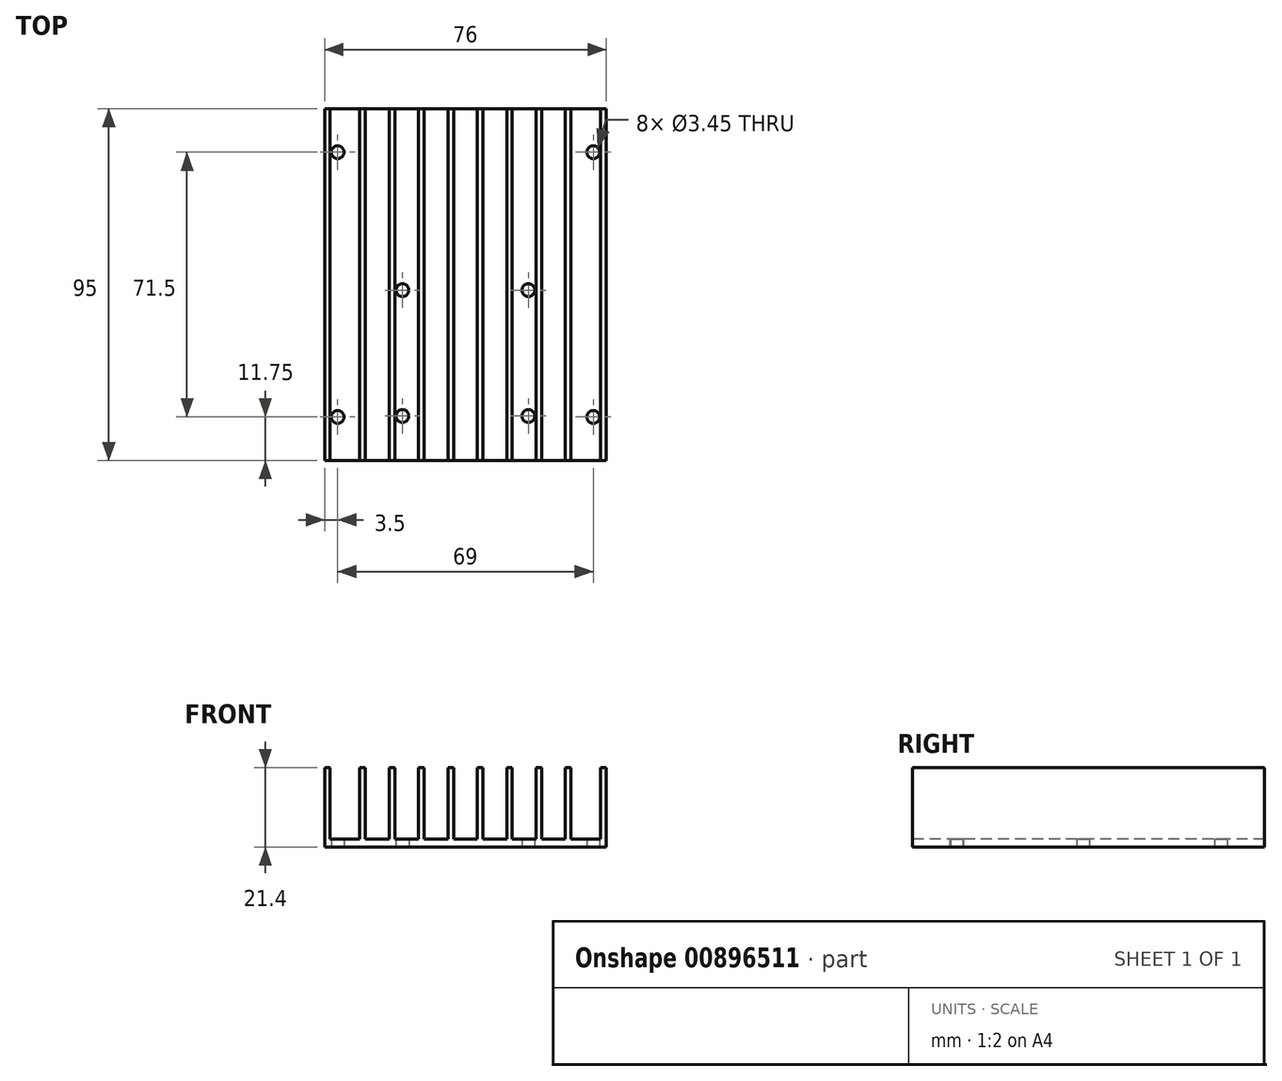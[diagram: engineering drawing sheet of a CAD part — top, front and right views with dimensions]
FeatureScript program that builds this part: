
annotation { "Feature Type Name" : "Feature", "Feature Type Description" : "" }
export const myFeature = defineFeature(function(context is Context, id is Id, definition is map)
    precondition{}
    {
        {
            var Q0;
            Q0=qCreatedBy(makeId("Top.planeOp"),FACE);
            var sketch = newSketch(context, id + "F0", { "sketchPlane" : qUnion([Q0])});
            skLineSegment(sketch, "E0.bottom", {"start": v(38, 47.5) * mm, "end": v(-38, 47.5) * mm});
            skLineSegment(sketch, "E0.top", {"start": v(38, -47.5) * mm, "end": v(-38, -47.5) * mm});
            skLineSegment(sketch, "E0.left", {"start": v(38, 47.5) * mm, "end": v(38, -47.5) * mm});
            skLineSegment(sketch, "E0.right", {"start": v(-38, 47.5) * mm, "end": v(-38, -47.5) * mm});
            skPoint(sketch, "E0.middle", {"position": v(0, 0) * mm});
            skSolve(sketch);
        }
        {
            var Q0;
            Q0 = qSketchRegion(id + "F0", true);
            extrude(context, id + "F1", {"entities" : qUnion([Q0]), "depth" : 21.4 * mm, "offsetDistance" : 25 * mm});
        }
        {
            var Q0;
            Q0=makeQuery(id+"F1.opExtrude","SWEPT_FACE",FACE,{"disambiguationData":[OSD([sQuery(id+"F0.wireOp",EDGE,"E0.top")])]});
            var sketch = newSketch(context, id + "F2", { "sketchPlane" : qUnion([Q0])});
            skLineSegment(sketch, "E1.bottom", {"start": v(-36.5, 21.4) * mm, "end": v(-28.5, 21.4) * mm});
            skLineSegment(sketch, "E1.top", {"start": v(-36.5, 2.1) * mm, "end": v(-28.5, 2.1) * mm});
            skLineSegment(sketch, "E1.left", {"start": v(-36.5, 21.4) * mm, "end": v(-36.5, 2.1) * mm});
            skLineSegment(sketch, "E1.right", {"start": v(-28.5, 21.4) * mm, "end": v(-28.5, 2.1) * mm});
            skLineSegment(sketch, "E2.bottom", {"start": v(28.5, 21.4) * mm, "end": v(36.5, 21.4) * mm});
            skLineSegment(sketch, "E2.top", {"start": v(28.5, 2.1) * mm, "end": v(36.5, 2.1) * mm});
            skLineSegment(sketch, "E2.left", {"start": v(28.5, 21.4) * mm, "end": v(28.5, 2.1) * mm});
            skLineSegment(sketch, "E2.right", {"start": v(36.5, 21.4) * mm, "end": v(36.5, 2.1) * mm});
            skLineSegment(sketch, "E3.bottom", {"start": v(-27, 21.4) * mm, "end": v(-20.57, 21.4) * mm});
            skLineSegment(sketch, "E3.top", {"start": v(-27, 2.1) * mm, "end": v(-20.57, 2.1) * mm});
            skLineSegment(sketch, "E3.left", {"start": v(-27, 21.4) * mm, "end": v(-27, 2.1) * mm});
            skLineSegment(sketch, "E3.right", {"start": v(-20.57, 21.4) * mm, "end": v(-20.57, 2.1) * mm});
            skLineSegment(sketch, "E4.bottom", {"start": v(-19.07, 21.4) * mm, "end": v(-12.64, 21.4) * mm});
            skLineSegment(sketch, "E4.top", {"start": v(-19.07, 2.1) * mm, "end": v(-12.64, 2.1) * mm});
            skLineSegment(sketch, "E4.left", {"start": v(-19.07, 21.4) * mm, "end": v(-19.07, 2.1) * mm});
            skLineSegment(sketch, "E4.right", {"start": v(-12.64, 21.4) * mm, "end": v(-12.64, 2.1) * mm});
            skLineSegment(sketch, "E5.bottom", {"start": v(-11.14, 21.4) * mm, "end": v(-4.71, 21.4) * mm});
            skLineSegment(sketch, "E5.top", {"start": v(-11.14, 2.1) * mm, "end": v(-4.71, 2.1) * mm});
            skLineSegment(sketch, "E5.left", {"start": v(-11.14, 21.4) * mm, "end": v(-11.14, 2.1) * mm});
            skLineSegment(sketch, "E5.right", {"start": v(-4.71, 21.4) * mm, "end": v(-4.71, 2.1) * mm});
            skLineSegment(sketch, "E6.bottom", {"start": v(-3.21, 21.4) * mm, "end": v(3.21, 21.4) * mm});
            skLineSegment(sketch, "E6.top", {"start": v(-3.21, 2.1) * mm, "end": v(3.21, 2.1) * mm});
            skLineSegment(sketch, "E6.left", {"start": v(-3.21, 21.4) * mm, "end": v(-3.21, 2.1) * mm});
            skLineSegment(sketch, "E6.right", {"start": v(3.21, 21.4) * mm, "end": v(3.21, 2.1) * mm});
            skLineSegment(sketch, "E7.bottom", {"start": v(4.71, 21.4) * mm, "end": v(11.14, 21.4) * mm});
            skLineSegment(sketch, "E7.top", {"start": v(4.71, 2.1) * mm, "end": v(11.14, 2.1) * mm});
            skLineSegment(sketch, "E7.left", {"start": v(4.71, 21.4) * mm, "end": v(4.71, 2.1) * mm});
            skLineSegment(sketch, "E7.right", {"start": v(11.14, 21.4) * mm, "end": v(11.14, 2.1) * mm});
            skLineSegment(sketch, "E8.bottom", {"start": v(12.64, 21.4) * mm, "end": v(19.07, 21.4) * mm});
            skLineSegment(sketch, "E8.top", {"start": v(12.64, 2.1) * mm, "end": v(19.07, 2.1) * mm});
            skLineSegment(sketch, "E8.left", {"start": v(12.64, 21.4) * mm, "end": v(12.64, 2.1) * mm});
            skLineSegment(sketch, "E8.right", {"start": v(19.07, 21.4) * mm, "end": v(19.07, 2.1) * mm});
            skLineSegment(sketch, "E9.bottom", {"start": v(20.57, 21.4) * mm, "end": v(27, 21.4) * mm});
            skLineSegment(sketch, "E9.top", {"start": v(20.57, 2.1) * mm, "end": v(27, 2.1) * mm});
            skLineSegment(sketch, "E9.left", {"start": v(20.57, 21.4) * mm, "end": v(20.57, 2.1) * mm});
            skLineSegment(sketch, "E9.right", {"start": v(27, 21.4) * mm, "end": v(27, 2.1) * mm});
            skLineSegment(sketch, "E10", {"start": v(-28.5, 21.4) * mm, "end": v(-27, 21.4) * mm, "construction": true});
            skLineSegment(sketch, "E11", {"start": v(-20.57, 21.4) * mm, "end": v(-19.07, 21.4) * mm, "construction": true});
            skLineSegment(sketch, "E12", {"start": v(-12.64, 21.4) * mm, "end": v(-11.14, 21.4) * mm, "construction": true});
            skLineSegment(sketch, "E13", {"start": v(-4.71, 21.4) * mm, "end": v(-3.21, 21.4) * mm, "construction": true});
            skLineSegment(sketch, "E14", {"start": v(3.21, 21.4) * mm, "end": v(4.71, 21.4) * mm, "construction": true});
            skLineSegment(sketch, "E15", {"start": v(11.14, 21.4) * mm, "end": v(12.64, 21.4) * mm, "construction": true});
            skLineSegment(sketch, "E16", {"start": v(19.07, 21.4) * mm, "end": v(20.57, 21.4) * mm, "construction": true});
            skLineSegment(sketch, "E17", {"start": v(27, 21.4) * mm, "end": v(28.5, 21.4) * mm, "construction": true});
            skSolve(sketch);
        }
        {
            var Q0;
            Q0 = qSketchRegion(id + "F2", true);
            extrude(context, id + "F3", {"entities" : qUnion([Q0]), "operationType" : NewBodyOperationType.REMOVE, "endBound" : BoundingType.UP_TO_NEXT, "oppositeDirection" : true, "depth" : 25 * mm, "offsetDistance" : 25 * mm});
        }
        {
            var Q0;
            Q0=makeQuery(id+"F1.opExtrude","CAP_FACE",FACE,{"disambiguationData":[OSD([sQuery(id+"F0.wireOp",EDGE,"E0.bottom"),sQuery(id+"F0.wireOp",EDGE,"E0.top"),sQuery(id+"F0.wireOp",EDGE,"E0.left"),sQuery(id+"F0.wireOp",EDGE,"E0.right")])],"isStart":true});
            var sketch = newSketch(context, id + "F4", { "sketchPlane" : qUnion([Q0])});
            skLineSegment(sketch, "E18.bottom", {"start": v(-17, 35.5) * mm, "end": v(17, 35.5) * mm, "construction": true});
            skLineSegment(sketch, "E18.top", {"start": v(-17, 1.5) * mm, "end": v(17, 1.5) * mm, "construction": true});
            skLineSegment(sketch, "E18.left", {"start": v(-17, 35.5) * mm, "end": v(-17, 1.5) * mm, "construction": true});
            skLineSegment(sketch, "E18.right", {"start": v(17, 35.5) * mm, "end": v(17, 1.5) * mm, "construction": true});
            skLineSegment(sketch, "E19", {"start": v(0, 47.5) * mm, "end": v(0, 35.5) * mm, "construction": true});
            skCircle(sketch, "E20", {"center": v(-17, 35.5) * mm, "radius": 1.73 * mm});
            skCircle(sketch, "E21", {"center": v(17, 35.5) * mm, "radius": 1.73 * mm});
            skCircle(sketch, "E22", {"center": v(17, 1.5) * mm, "radius": 1.73 * mm});
            skCircle(sketch, "E23", {"center": v(-17, 1.5) * mm, "radius": 1.73 * mm});
            skLineSegment(sketch, "E24.bottom", {"start": v(34.5, 35.75) * mm, "end": v(-34.5, 35.75) * mm, "construction": true});
            skLineSegment(sketch, "E24.top", {"start": v(34.5, -35.75) * mm, "end": v(-34.5, -35.75) * mm, "construction": true});
            skLineSegment(sketch, "E24.left", {"start": v(34.5, 35.75) * mm, "end": v(34.5, -35.75) * mm, "construction": true});
            skLineSegment(sketch, "E24.right", {"start": v(-34.5, 35.75) * mm, "end": v(-34.5, -35.75) * mm, "construction": true});
            skPoint(sketch, "E24.middle", {"position": v(0, 0) * mm});
            skCircle(sketch, "E25", {"center": v(-34.5, 35.75) * mm, "radius": 1.73 * mm});
            skCircle(sketch, "E26", {"center": v(34.5, 35.75) * mm, "radius": 1.73 * mm});
            skCircle(sketch, "E27", {"center": v(34.5, -35.75) * mm, "radius": 1.73 * mm});
            skCircle(sketch, "E28", {"center": v(-34.5, -35.75) * mm, "radius": 1.73 * mm});
            skSolve(sketch);
        }
        {
            var Q0;
            Q0 = qSketchRegion(id + "F4", true);
            extrude(context, id + "F5", {"entities" : qUnion([Q0]), "operationType" : NewBodyOperationType.REMOVE, "endBound" : BoundingType.UP_TO_NEXT, "oppositeDirection" : true, "depth" : 25 * mm, "offsetDistance" : 25 * mm});
        }
    });
